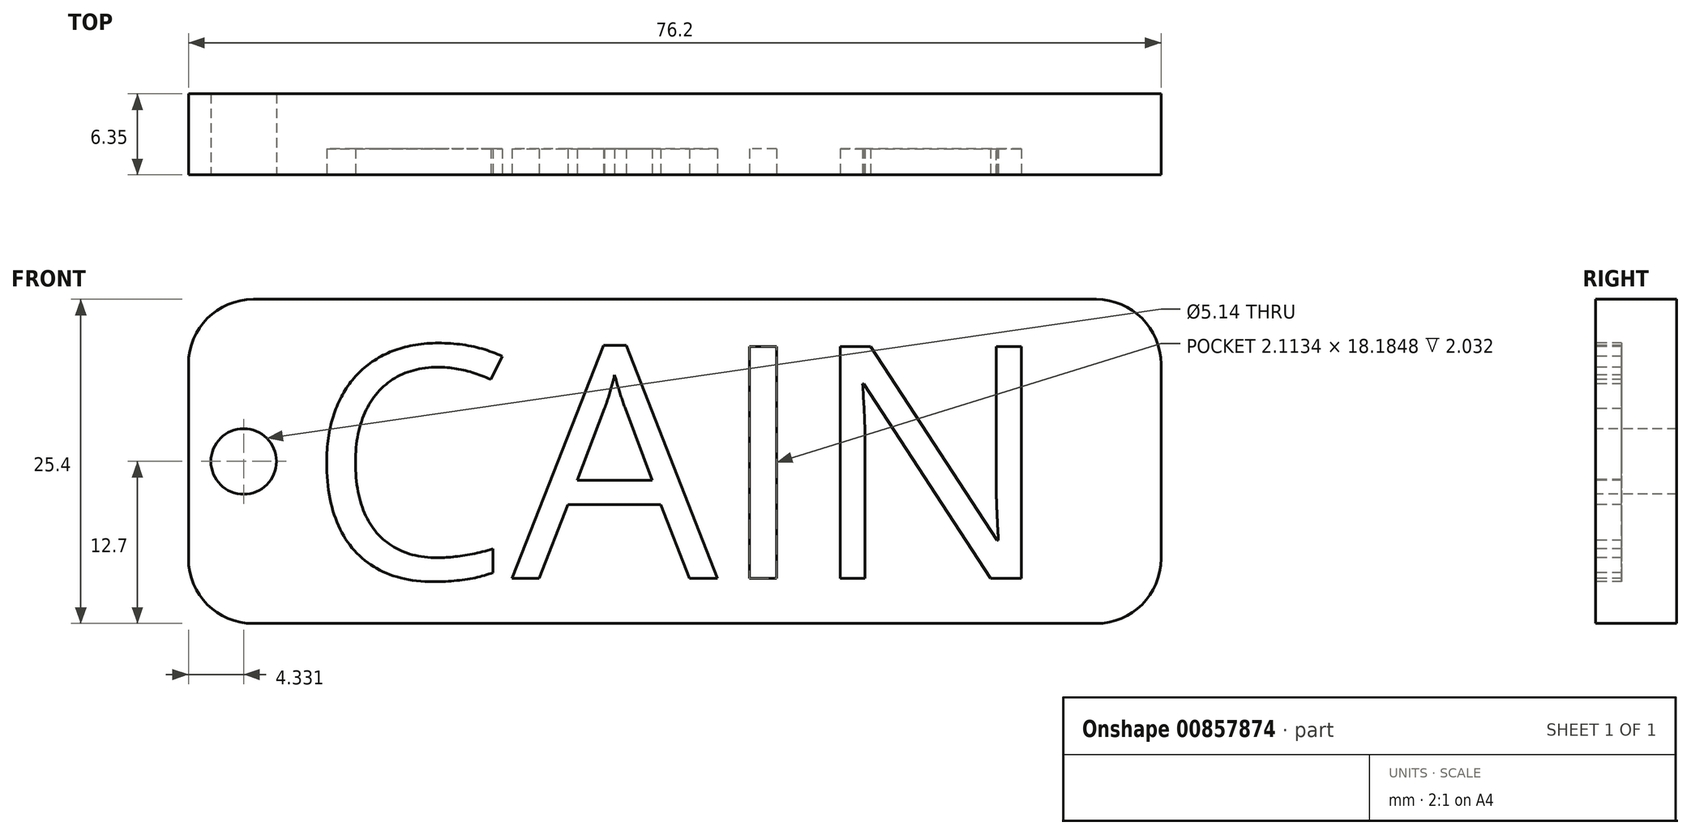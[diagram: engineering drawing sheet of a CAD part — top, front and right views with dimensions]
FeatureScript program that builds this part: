
annotation { "Feature Type Name" : "Feature", "Feature Type Description" : "" }
export const myFeature = defineFeature(function(context is Context, id is Id, definition is map)
    precondition{}
    {
        {
            var Q0;
            Q0=qCreatedBy(makeId("Front.planeOp"),FACE);
            var sketch = newSketch(context, id + "F0", { "sketchPlane" : qUnion([Q0])});
            skLineSegment(sketch, "E0.bottom", {"start": v(-38.1, 12.7) * mm, "end": v(38.1, 12.7) * mm});
            skLineSegment(sketch, "E0.top", {"start": v(-38.1, -12.7) * mm, "end": v(38.1, -12.7) * mm});
            skLineSegment(sketch, "E0.left", {"start": v(-38.1, 12.7) * mm, "end": v(-38.1, -12.7) * mm});
            skLineSegment(sketch, "E0.right", {"start": v(38.1, 12.7) * mm, "end": v(38.1, -12.7) * mm});
            skPoint(sketch, "E0.middle", {"position": v(0, 0) * mm});
            skSolve(sketch);
        }
        {
            var Q0;
            Q0 = qSketchRegion(id + "F0", true);
            extrude(context, id + "F1", {"entities" : qUnion([Q0]), "oppositeDirection" : true, "depth" : 6.35 * mm, "offsetDistance" : 25.4 * mm});
        }
        {
            var Q0;
            Q0=makeQuery(id+"F1.opExtrude","SWEPT_EDGE",EDGE,{"disambiguationData":[OSD([sQuery(id+"F0.wireOp",EDGE,"E0.bottom"),sQuery(id+"F0.wireOp",EDGE,"E0.left")])]});
            var Q1;
            Q1=makeQuery(id+"F1.opExtrude","SWEPT_EDGE",EDGE,{"disambiguationData":[OSD([sQuery(id+"F0.wireOp",EDGE,"E0.top"),sQuery(id+"F0.wireOp",EDGE,"E0.left")])]});
            var Q2;
            Q2=makeQuery(id+"F1.opExtrude","SWEPT_EDGE",EDGE,{"disambiguationData":[OSD([sQuery(id+"F0.wireOp",EDGE,"E0.bottom"),sQuery(id+"F0.wireOp",EDGE,"E0.right")])]});
            var Q3;
            Q3=makeQuery(id+"F1.opExtrude","SWEPT_EDGE",EDGE,{"disambiguationData":[OSD([sQuery(id+"F0.wireOp",EDGE,"E0.top"),sQuery(id+"F0.wireOp",EDGE,"E0.right")])]});
            fillet(context, id + "F2", {"entities" : qUnion([Q0, Q1, Q2, Q3]), "radius" : 5.08 * mm, "tangentPropagation" : true, "allowEdgeOverflow" : false});
        }
        {
            var Q0;
            Q0=qCreatedBy(makeId("Front.planeOp"),FACE);
            var sketch = newSketch(context, id + "F3", { "sketchPlane" : qUnion([Q0])});
            skText(sketch, "E1", { "text": "CAIN", "fontName": "OpenSans-Regular.ttf"});
            const initialGuessF3  = {"E1": [-0.02883, -0.00917, 1, 0, 0.01834]};
            skSetInitialGuess(sketch, initialGuessF3);
            skSolve(sketch);
        }
        {
            var Q0;
            Q0 = qSketchRegion(id + "F3", true);
            extrude(context, id + "F4", {"entities" : qUnion([Q0]), "operationType" : NewBodyOperationType.REMOVE, "oppositeDirection" : true, "depth" : 2.03 * mm, "offsetDistance" : 25.4 * mm});
        }
        {
            var Q0;
            Q0=qCreatedBy(makeId("Front.planeOp"),FACE);
            var sketch = newSketch(context, id + "F5", { "sketchPlane" : qUnion([Q0])});
            skCircle(sketch, "E2", {"center": v(-33.77, 0) * mm, "radius": 2.57 * mm});
            skSolve(sketch);
        }
        {
            var Q0;
            Q0 = qSketchRegion(id + "F5", true);
            extrude(context, id + "F6", {"entities" : qUnion([Q0]), "operationType" : NewBodyOperationType.REMOVE, "oppositeDirection" : true, "depth" : 25.4 * mm, "offsetDistance" : 25.4 * mm});
        }
    });
